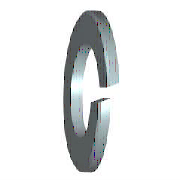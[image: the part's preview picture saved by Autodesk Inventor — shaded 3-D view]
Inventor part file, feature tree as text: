
AUTODESK INVENTOR PART (.ipt)
format: ipt  version: 2021.2 (Build 252289000, 289)  size: 133,120 bytes
history: native  units: mm
features: sketch x2, other x1, plane x1
ambient origin geometry x8: Origin, YZ Plane, XZ Plane, XY Plane, X Axis, Y Axis, Z Axis, Center Point
bodies: Solid1 (feature_tree)
feature tree (4):
  other  "Work Axis1"
  plane  "Work Plane1"
  sketch  "Sketch1"  dims[d0=6.9mm]
  sketch  "Sketch2"  dims[d1=4.1mm d2=1.0mm d3=0.0mm d4=12.217305mm d7=1.0mm d8=0.0mm d9=0.0mm d10=0.0mm d11=0.0mm d12=0.0mm d13=0.5mm]
